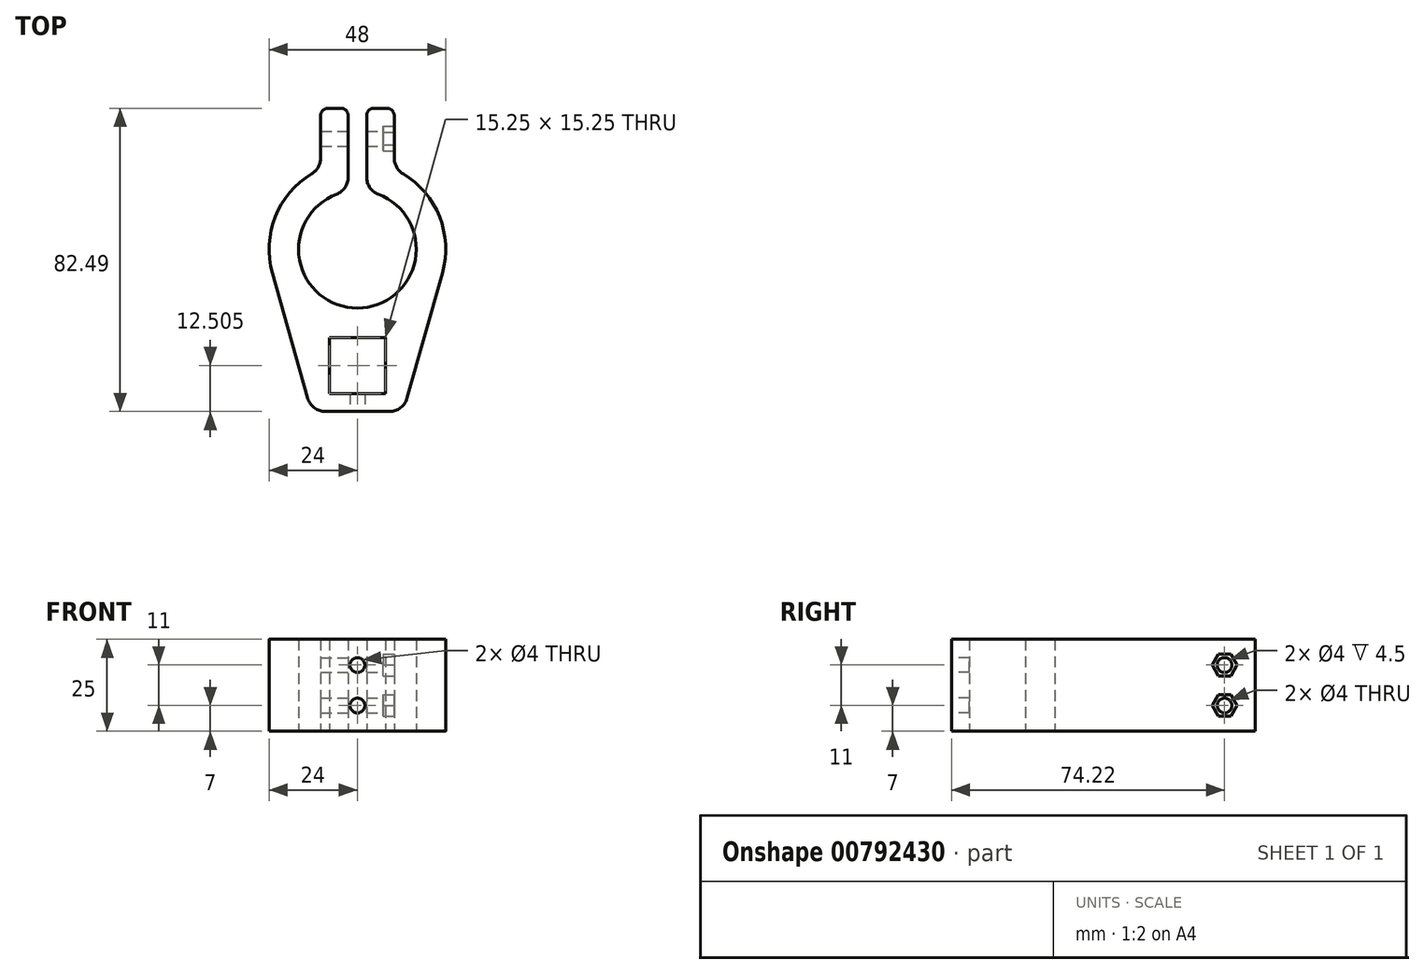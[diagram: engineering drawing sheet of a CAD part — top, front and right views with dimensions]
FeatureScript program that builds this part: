
annotation { "Feature Type Name" : "Feature", "Feature Type Description" : "" }
export const myFeature = defineFeature(function(context is Context, id is Id, definition is map)
    precondition{}
    {
        {
            var Q0;
            Q0=qCreatedBy(makeId("Top.planeOp"),FACE);
            var sketch = newSketch(context, id + "F0", { "sketchPlane" : qUnion([Q0])});
            skCircle(sketch, "E0", {"center": v(0, 0) * mm, "radius": 16 * mm});
            skCircle(sketch, "E1", {"center": v(0, 0) * mm, "radius": 24 * mm});
            skLineSegment(sketch, "E2", {"start": v(-2.5, 0) * mm, "end": v(-2.5, 49.83) * mm});
            skLineSegment(sketch, "E3", {"start": v(-2.5, 49.83) * mm, "end": v(2.5, 49.83) * mm});
            skLineSegment(sketch, "E4", {"start": v(2.5, 49.83) * mm, "end": v(2.5, 0) * mm});
            skLineSegment(sketch, "E5", {"start": v(2.5, 0) * mm, "end": v(-2.5, 0) * mm});
            skLineSegment(sketch, "E6.bottom", {"start": v(-10, 0) * mm, "end": v(10, 0) * mm});
            skLineSegment(sketch, "E6.top", {"start": v(-10, 38.36) * mm, "end": v(10, 38.36) * mm});
            skLineSegment(sketch, "E6.left", {"start": v(-10, 0) * mm, "end": v(-10, 38.36) * mm});
            skLineSegment(sketch, "E6.right", {"start": v(10, 0) * mm, "end": v(10, 38.36) * mm});
            skLineSegment(sketch, "E7.bottom", {"start": v(7.62, -24) * mm, "end": v(-7.62, -24) * mm});
            skLineSegment(sketch, "E7.top", {"start": v(7.62, -39.25) * mm, "end": v(-7.62, -39.25) * mm});
            skLineSegment(sketch, "E7.left", {"start": v(7.62, -24) * mm, "end": v(7.62, -39.25) * mm});
            skLineSegment(sketch, "E7.right", {"start": v(-7.63, -24) * mm, "end": v(-7.63, -39.25) * mm});
            skPoint(sketch, "E8", {"position": v(0, -24) * mm});
            skLineSegment(sketch, "E9.bottom", {"start": v(-12.5, -19.12) * mm, "end": v(12.5, -19.12) * mm});
            skLineSegment(sketch, "E9.top", {"start": v(-12.5, -44.12) * mm, "end": v(12.5, -44.12) * mm});
            skLineSegment(sketch, "E9.left", {"start": v(-12.5, -19.13) * mm, "end": v(-12.5, -44.12) * mm});
            skLineSegment(sketch, "E9.right", {"start": v(12.5, -19.13) * mm, "end": v(12.5, -44.12) * mm});
            skPoint(sketch, "E10", {"position": v(0, -19.12) * mm});
            skPoint(sketch, "E11", {"position": v(7.62, -31.62) * mm});
            skPoint(sketch, "E12", {"position": v(12.5, -31.62) * mm});
            skLineSegment(sketch, "E13", {"start": v(39.26, -31.62) * mm, "end": v(-45.33, -31.62) * mm, "construction": true});
            skLineSegment(sketch, "E14", {"start": v(-12.5, -44.12) * mm, "end": v(-23.1, -6.5) * mm});
            skLineSegment(sketch, "E15", {"start": v(12.5, -44.12) * mm, "end": v(23.1, -6.5) * mm});
            skSolve(sketch);
        }
        {
            var Q0;
            {var subQ11=sQuery(id+"F0.wireOp",EDGE,"E9.bottom");Q0=makeQuery(id+"F0.imprint","IMPRINT",FACE,{"disambiguationData":[TD([[makeQuery(id+"F0.imprint","IMPRINT",EDGE,{"derivedFrom":subQ11}),1.0]])]});}
            var Q1;
            {var subQ0=sQuery(id+"F0.wireOp",EDGE,"E2");var subQ1=sQuery(id+"F0.wireOp",EDGE,"E0");var subQ2=makeQuery(id+"F0.imprint","INTERSECT",VERTEX,{"derivedFrom":[subQ1,subQ0]});Q1=makeQuery(id+"F0.imprint","IMPRINT",FACE,{"disambiguationData":[TD([[makeQuery(id+"F0.imprint","IMPRINT",EDGE,{"disambiguationData":[TD([[subQ2,-1.0]])],"derivedFrom":subQ1}),-1.0]])]});}
            var Q2;
            {var subQ0=sQuery(id+"F0.wireOp",EDGE,"E6.left");var subQ1=sQuery(id+"F0.wireOp",EDGE,"E1");var subQ2=makeQuery(id+"F0.imprint","INTERSECT",VERTEX,{"derivedFrom":[subQ1,subQ0]});Q2=makeQuery(id+"F0.imprint","IMPRINT",FACE,{"disambiguationData":[TD([[makeQuery(id+"F0.imprint","IMPRINT",EDGE,{"disambiguationData":[TD([[subQ2,1.0]])],"derivedFrom":subQ1}),-1.0]])]});}
            var Q3;
            {var subQ0=sQuery(id+"F0.wireOp",EDGE,"E4");var subQ1=sQuery(id+"F0.wireOp",EDGE,"E0");var subQ2=makeQuery(id+"F0.imprint","INTERSECT",VERTEX,{"derivedFrom":[subQ1,subQ0]});Q3=makeQuery(id+"F0.imprint","IMPRINT",FACE,{"disambiguationData":[TD([[makeQuery(id+"F0.imprint","IMPRINT",EDGE,{"disambiguationData":[TD([[subQ2,1.0]])],"derivedFrom":subQ1}),-1.0]])]});}
            var Q4;
            {var subQ0=sQuery(id+"F0.wireOp",EDGE,"E6.right");var subQ1=sQuery(id+"F0.wireOp",EDGE,"E1");var subQ2=makeQuery(id+"F0.imprint","INTERSECT",VERTEX,{"derivedFrom":[subQ1,subQ0]});Q4=makeQuery(id+"F0.imprint","IMPRINT",FACE,{"disambiguationData":[TD([[makeQuery(id+"F0.imprint","IMPRINT",EDGE,{"disambiguationData":[TD([[subQ2,-1.0]])],"derivedFrom":subQ1}),-1.0]])]});}
            var Q5;
            {var subQ1=sQuery(id+"F0.wireOp",EDGE,"E9.bottom");Q5=makeQuery(id+"F0.imprint","IMPRINT",FACE,{"disambiguationData":[TD([[makeQuery(id+"F0.imprint","IMPRINT",EDGE,{"derivedFrom":subQ1}),-1.0]])]});}
            var Q6;
            {var subQ0=sQuery(id+"F0.wireOp",EDGE,"E14");Q6=makeQuery(id+"F0.imprint","IMPRINT",FACE,{"disambiguationData":[TD([[makeQuery(id+"F0.imprint","IMPRINT",EDGE,{"derivedFrom":subQ0}),-1.0]])]});}
            var Q7;
            Q7=makeQuery(id+"F0.imprint","IMPRINT",FACE,{"disambiguationData":[TD([[makeQuery(id+"F0.imprint","IMPRINT",EDGE,{"derivedFrom":sQuery(id+"F0.wireOp",EDGE,"E7.top")}),1.0]])]});
            var Q8;
            {var subQ0=sQuery(id+"F0.wireOp",EDGE,"E15");Q8=makeQuery(id+"F0.imprint","IMPRINT",FACE,{"disambiguationData":[TD([[makeQuery(id+"F0.imprint","IMPRINT",EDGE,{"derivedFrom":subQ0}),1.0]])]});}
            extrude(context, id + "F1", {"entities" : qUnion([Q0, Q1, Q2, Q3, Q4, Q5, Q6, Q7, Q8]), "depth" : 25 * mm, "offsetDistance" : 25 * mm});
        }
        {
            var Q0;
            Q0=makeQuery(id+"F1.opExtrude","SWEPT_FACE",FACE,{"disambiguationData":[OSD([sQuery(id+"F0.wireOp",EDGE,"E6.right")])]});
            var sketch = newSketch(context, id + "F2", { "sketchPlane" : qUnion([Q0])});
            skCircle(sketch, "E16", {"center": v(30.1, 7) * mm, "radius": 2 * mm});
            skPoint(sketch, "E16.centerSnap0", {"position": v(30.1, 0) * mm});
            skCircle(sketch, "E17", {"center": v(30.1, 18) * mm, "radius": 2 * mm});
            skPoint(sketch, "E17.centerSnap0", {"position": v(30.1, 25) * mm});
            skCircle(sketch, "E18.cCircle", {"center": v(30.1, 18) * mm, "radius": 2.92 * mm, "construction": true});
            skLineSegment(sketch, "E18.0", {"start": v(31.78, 20.93) * mm, "end": v(33.47, 18) * mm});
            skLineSegment(sketch, "E18.1", {"start": v(33.47, 18) * mm, "end": v(31.78, 15.07) * mm});
            skLineSegment(sketch, "E18.2", {"start": v(31.78, 15.08) * mm, "end": v(28.4, 15.08) * mm});
            skLineSegment(sketch, "E18.3", {"start": v(28.4, 15.08) * mm, "end": v(26.71, 18) * mm});
            skLineSegment(sketch, "E18.4", {"start": v(26.71, 18) * mm, "end": v(28.4, 20.93) * mm});
            skLineSegment(sketch, "E18.5", {"start": v(28.4, 20.93) * mm, "end": v(31.78, 20.93) * mm});
            skPoint(sketch, "E18.0.midPoint", {"position": v(32.62, 19.46) * mm});
            skCircle(sketch, "E19.cCircle", {"center": v(30.1, 7) * mm, "radius": 2.93 * mm, "construction": true});
            skLineSegment(sketch, "E19.0", {"start": v(31.78, 9.93) * mm, "end": v(33.47, 7) * mm});
            skLineSegment(sketch, "E19.1", {"start": v(33.47, 7) * mm, "end": v(31.78, 4.08) * mm});
            skLineSegment(sketch, "E19.2", {"start": v(31.78, 4.08) * mm, "end": v(28.4, 4.07) * mm});
            skLineSegment(sketch, "E19.3", {"start": v(28.4, 4.07) * mm, "end": v(26.71, 7) * mm});
            skLineSegment(sketch, "E19.4", {"start": v(26.71, 7) * mm, "end": v(28.4, 9.92) * mm});
            skLineSegment(sketch, "E19.5", {"start": v(28.4, 9.92) * mm, "end": v(31.78, 9.93) * mm});
            skPoint(sketch, "E19.0.midPoint", {"position": v(32.62, 8.47) * mm});
            skSolve(sketch);
        }
        {
            var Q0;
            Q0=makeQuery(id+"F1.opExtrude","SWEPT_FACE",FACE,{"disambiguationData":[OSD([sQuery(id+"F0.wireOp",EDGE,"E9.top")])]});
            var sketch = newSketch(context, id + "F3", { "sketchPlane" : qUnion([Q0])});
            skCircle(sketch, "E20", {"center": v(0, 7) * mm, "radius": 2 * mm});
            skCircle(sketch, "E21", {"center": v(0, 18) * mm, "radius": 2 * mm});
            skSolve(sketch);
        }
        {
            var Q0;
            Q0 = qSketchRegion(id + "F3", true);
            extrude(context, id + "F4", {"entities" : qUnion([Q0]), "operationType" : NewBodyOperationType.REMOVE, "oppositeDirection" : true, "depth" : 10 * mm, "offsetDistance" : 25 * mm});
        }
        {
            var Q0;
            Q0=makeQuery(id+"F2.imprint","IMPRINT",FACE,{"disambiguationData":[TD([[makeQuery(id+"F2.imprint","IMPRINT",EDGE,{"derivedFrom":sQuery(id+"F2.wireOp",EDGE,"E17")}),1.0]])]});
            var Q1;
            Q1=makeQuery(id+"F2.imprint","IMPRINT",FACE,{"disambiguationData":[TD([[makeQuery(id+"F2.imprint","IMPRINT",EDGE,{"derivedFrom":sQuery(id+"F2.wireOp",EDGE,"E16")}),1.0]])]});
            extrude(context, id + "F5", {"entities" : qUnion([Q0, Q1]), "operationType" : NewBodyOperationType.REMOVE, "oppositeDirection" : true, "depth" : 50 * mm, "offsetDistance" : 25 * mm});
        }
        {
            var Q0;
            Q0=makeQuery(id+"F1.opExtrude","SWEPT_EDGE",EDGE,{"disambiguationData":[OSD([sQuery(id+"F0.wireOp",EDGE,"E9.top"),sQuery(id+"F0.wireOp",EDGE,"E9.right"),sQuery(id+"F0.wireOp",EDGE,"E15")])]});
            var Q1;
            Q1=makeQuery(id+"F1.opExtrude","SWEPT_EDGE",EDGE,{"disambiguationData":[OSD([sQuery(id+"F0.wireOp",EDGE,"E9.top"),sQuery(id+"F0.wireOp",EDGE,"E9.left"),sQuery(id+"F0.wireOp",EDGE,"E14")])]});
            var Q2;
            Q2=makeQuery(id+"F1.opExtrude","SWEPT_EDGE",EDGE,{"disambiguationData":[OSD([sQuery(id+"F0.wireOp",EDGE,"E1"),sQuery(id+"F0.wireOp",EDGE,"E6.right")])]});
            var Q3;
            Q3=makeQuery(id+"F1.opExtrude","SWEPT_EDGE",EDGE,{"disambiguationData":[OSD([sQuery(id+"F0.wireOp",EDGE,"E1"),sQuery(id+"F0.wireOp",EDGE,"E6.left")])]});
            var Q4;
            Q4=makeQuery(id+"F1.opExtrude","SWEPT_EDGE",EDGE,{"disambiguationData":[OSD([sQuery(id+"F0.wireOp",EDGE,"E0"),sQuery(id+"F0.wireOp",EDGE,"E2")])]});
            var Q5;
            Q5=makeQuery(id+"F1.opExtrude","SWEPT_EDGE",EDGE,{"disambiguationData":[OSD([sQuery(id+"F0.wireOp",EDGE,"E0"),sQuery(id+"F0.wireOp",EDGE,"E4")])]});
            fillet(context, id + "F6", {"entities" : qUnion([Q0, Q1, Q2, Q3, Q4, Q5]), "radius" : 5 * mm, "tangentPropagation" : true, "allowEdgeOverflow" : false});
        }
        {
            var Q0;
            Q0=makeQuery(id+"F1.opExtrude","SWEPT_EDGE",EDGE,{"disambiguationData":[OSD([sQuery(id+"F0.wireOp",EDGE,"E6.top"),sQuery(id+"F0.wireOp",EDGE,"E6.right")])]});
            var Q1;
            Q1=makeQuery(id+"F1.opExtrude","SWEPT_EDGE",EDGE,{"disambiguationData":[OSD([sQuery(id+"F0.wireOp",EDGE,"E6.top"),sQuery(id+"F0.wireOp",EDGE,"E6.left")])]});
            var Q2;
            Q2=makeQuery(id+"F1.opExtrude","SWEPT_EDGE",EDGE,{"disambiguationData":[OSD([sQuery(id+"F0.wireOp",EDGE,"E2"),sQuery(id+"F0.wireOp",EDGE,"E6.top")])]});
            var Q3;
            Q3=makeQuery(id+"F1.opExtrude","SWEPT_EDGE",EDGE,{"disambiguationData":[OSD([sQuery(id+"F0.wireOp",EDGE,"E4"),sQuery(id+"F0.wireOp",EDGE,"E6.top")])]});
            fillet(context, id + "F7", {"entities" : qUnion([Q0, Q1, Q2, Q3]), "radius" : 2 * mm, "tangentPropagation" : true, "allowEdgeOverflow" : false});
        }
        {
            var Q0;
            Q0 = qSketchRegion(id + "F2", true);
            extrude(context, id + "F8", {"entities" : qUnion([Q0]), "operationType" : NewBodyOperationType.REMOVE, "oppositeDirection" : true, "depth" : 3 * mm, "offsetDistance" : 25 * mm});
        }
    });
